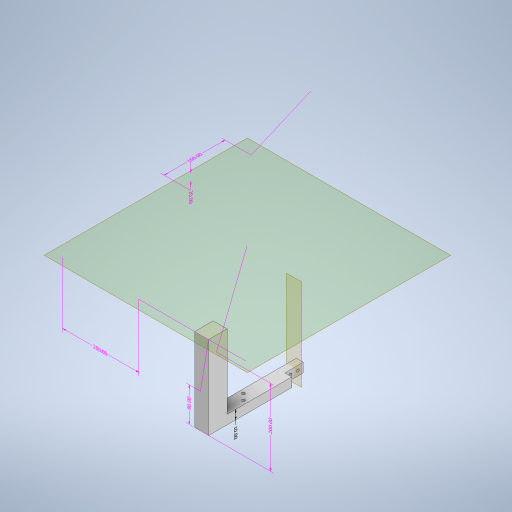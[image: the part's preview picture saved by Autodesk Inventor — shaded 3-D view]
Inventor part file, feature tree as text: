
AUTODESK INVENTOR PART (.ipt)
format: ipt  version: 2023 (Build 270158000, 158)  size: 391,680 bytes
history: native  units: mm
features: sketch x9, other x8, extrude x5, hole x3, plane x2, split x2
ambient origin geometry x8: Origin, YZ Plane, XZ Plane, XY Plane, X Axis, Y Axis, Z Axis, Center Point
bodies: Body1 (feature_tree)
feature tree (29):
  other  "Sólido1"
  other  "Anotaciones"
  extrude  "Extrusión1"  Depth=15.0mm
  hole  "Agujero1"  [1 undecoded]
  extrude  "Extrusión2"  Depth=15.0mm
  extrude  "Extrusión3"  Depth=80.0mm TaperAngle=0.0deg
  extrude  "Extrusión4"  Depth=200.0mm
  extrude  "Extrusión5"  Depth=20.0mm
  hole  "Agujero2"  [1 undecoded]
  plane  "Plano de trabajo1"
  split  "Dividir1"
  plane  "Plano de trabajo2"
  hole  "Agujero3"  [1 undecoded]
  split  "Dividir2"
  sketch  "Boceto2"  dims[d7=15.0mm d8=200.0mm]
  sketch  "Boceto3"  dims[d9=10.0mm d10=0.0mm]
  sketch  "Boceto4"  dims[d11=3.5mm d12=1.75mm d13=1.75mm d14=1.75mm d15=1.75mm d16=10.0mm d17=10.0mm d19=40.0mm]
  sketch  "Boceto5"  dims[d20=3.5mm d21=6.0mm d22=4.0mm d23=2.0mm d24=90.0deg d25=8.0mm d26=20.594885mm d27=15.0mm]
  sketch  "Boceto6"  dims[d28=20.0mm d29=80.0mm d30=0.0mm]
  sketch  "Boceto7"  dims[d31=57.0mm d32=200.0mm]
  sketch  "Boceto8"  dims[d33=110.0mm d34=0.0mm d36=20.0mm]
  sketch  "Boceto9"  dims[d37=20.0mm d38=20.0mm]
  sketch  "Boceto10"  dims[d39=90.0mm d40=0.0mm d43=30.0mm d44=0.0mm d45=3.5mm d46=1.75mm d47=1.75mm d48=1.75mm d49=1.75mm d50=10.0mm d51=10.0mm d52=15.0mm d53=10.0mm d54=10.0mm d55=15.0mm d56=3.5mm d57=6.0mm d58=4.0mm d59=2.0mm d60=90.0deg d61=8.0mm d62=20.594885mm d63=10.0mm d65=10.0mm d75=200.0mm d76=10.0mm d77=20.0mm d81=40.0mm d88=90.0deg d89=3.5mm d90=3.5mm d91=6.0mm d92=4.0mm d93=2.0mm d94=90.0deg d95=8.0mm d96=20.594885mm d97=10.0mm d98=10.0mm d66=5.760865mm d67=7.72461mm d68=200.0mm d69=3.008686mm d70=2.422102mm d71=10.0mm d72=3.500509mm d73=2.402572mm d74=90.0mm d78=3.13122mm d79=6.269346mm d80=200.0mm d82=8.450127mm d83=0.968417mm d84=20.0mm d85=4.759975mm d86=4.646891mm d87=160.0mm]
  other  "Cota lineal 1"
  other  "Cota lineal 2"
  other  "Cota lineal 3"
  other  "Cota lineal 4"
  other  "Cota lineal 5"
  other  "Cota lineal 6"
note: 3 required parameter values undecoded (feature->parameter linkage not recoverable at this tier; creation-order binding heuristic only, values carry confidence <= 0.55)
